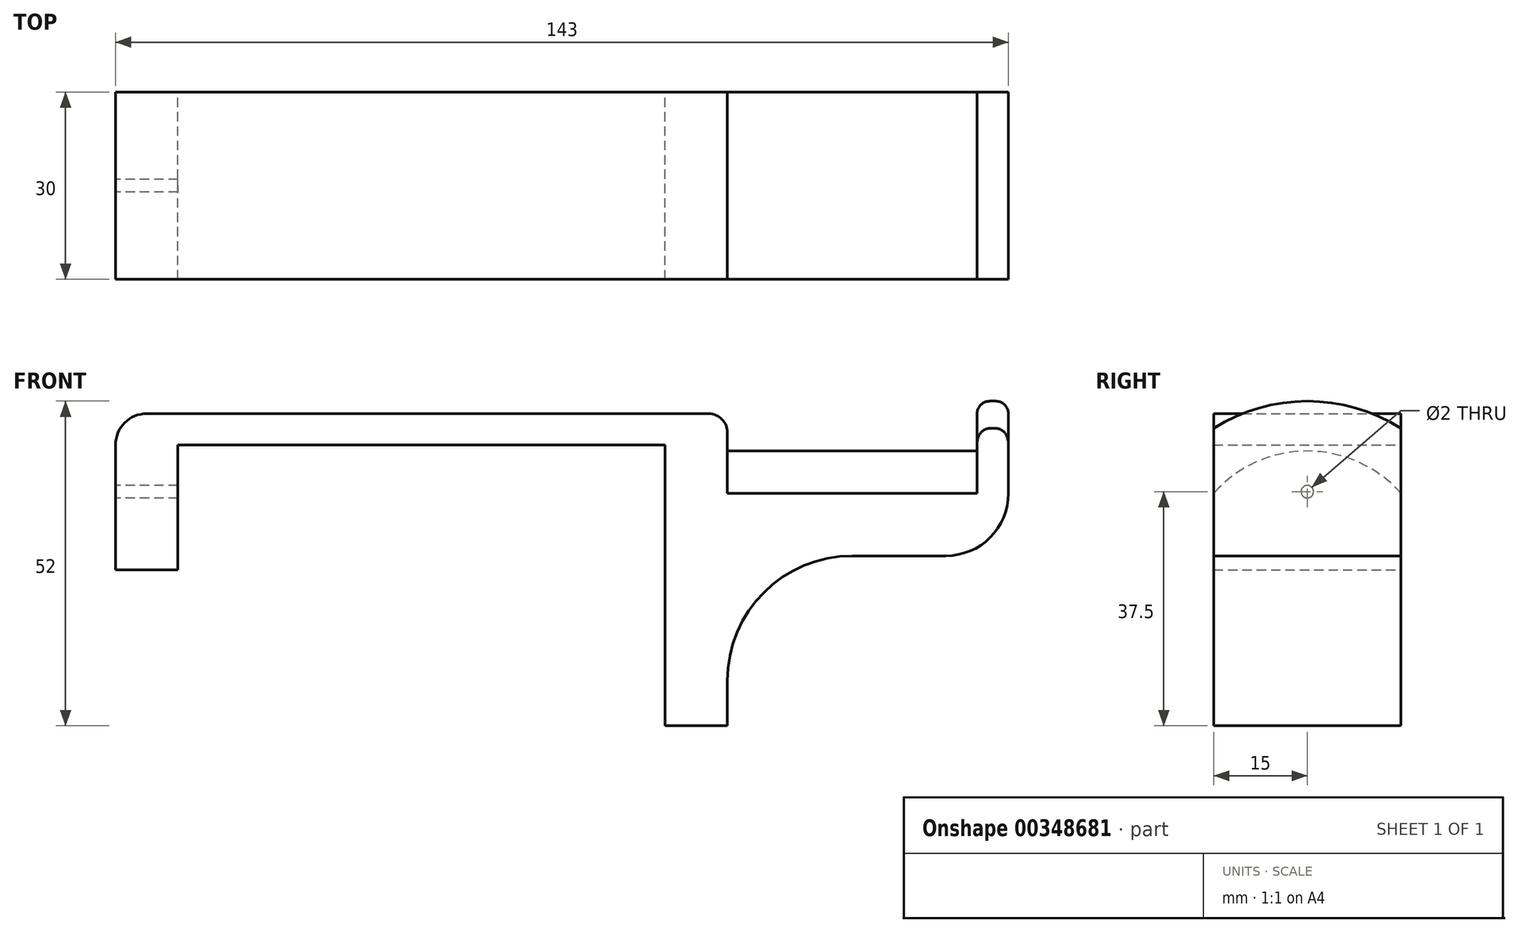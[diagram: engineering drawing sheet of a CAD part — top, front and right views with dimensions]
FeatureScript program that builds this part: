
annotation { "Feature Type Name" : "Feature", "Feature Type Description" : "" }
export const myFeature = defineFeature(function(context is Context, id is Id, definition is map)
    precondition{}
    {
        {
            var Q0;
            Q0=qCreatedBy(makeId("Front.planeOp"),FACE);
            var sketch = newSketch(context, id + "F0", { "sketchPlane" : qUnion([Q0])});
            skLineSegment(sketch, "E0", {"start": v(0, 0) * mm, "end": v(0, 45) * mm});
            skLineSegment(sketch, "E1", {"start": v(0, 45) * mm, "end": v(-78, 45) * mm});
            skLineSegment(sketch, "E2", {"start": v(-78, 45) * mm, "end": v(-78, 25) * mm});
            skLineSegment(sketch, "E3", {"start": v(-78, 25) * mm, "end": v(-88, 25) * mm});
            skLineSegment(sketch, "E4", {"start": v(-88, 25) * mm, "end": v(-88, 50) * mm});
            skLineSegment(sketch, "E5", {"start": v(-88, 50) * mm, "end": v(10, 50) * mm});
            skLineSegment(sketch, "E6", {"start": v(10, 50) * mm, "end": v(10, 0) * mm});
            skLineSegment(sketch, "E7", {"start": v(10, 0) * mm, "end": v(0, 0) * mm});
            skSolve(sketch);
        }
        {
            var Q0;
            Q0=makeQuery(id+"F0.imprint","IMPRINT",FACE,{"disambiguationData":[TD([[makeQuery(id+"F0.imprint","IMPRINT",EDGE,{"derivedFrom":sQuery(id+"F0.wireOp",EDGE,"E0")}),-1.0]])]});
            extrude(context, id + "F1", {"entities" : qUnion([Q0]), "depth" : 30 * mm});
        }
        {
            var Q0;
            Q0=makeQuery(id+"F1.opExtrude","SWEPT_FACE",FACE,{"disambiguationData":[OSD([sQuery(id+"F0.wireOp",EDGE,"E4")])]});
            var sketch = newSketch(context, id + "F2", { "sketchPlane" : qUnion([Q0])});
            skLineSegment(sketch, "E8", {"start": v(15, 50) * mm, "end": v(15, 25) * mm, "construction": true});
            skCircle(sketch, "E9", {"center": v(15, 37.5) * mm, "radius": 1 * mm});
            skSolve(sketch);
        }
        {
            var Q0;
            Q0=makeQuery(id+"F2.imprint","IMPRINT",FACE,{"disambiguationData":[TD([[makeQuery(id+"F2.imprint","IMPRINT",EDGE,{"derivedFrom":sQuery(id+"F2.wireOp",EDGE,"E9")}),1.0]])]});
            extrude(context, id + "F3", {"entities" : qUnion([Q0]), "operationType" : NewBodyOperationType.REMOVE, "endBound" : BoundingType.UP_TO_NEXT, "oppositeDirection" : true, "depth" : 25 * mm});
        }
        {
            var Q0;
            Q0=makeQuery(id+"F1.opExtrude","SWEPT_FACE",FACE,{"disambiguationData":[OSD([sQuery(id+"F0.wireOp",EDGE,"E6")])]});
            var sketch = newSketch(context, id + "F4", { "sketchPlane" : qUnion([Q0])});
            skArc(sketch, "E10", {"start": v(0, 37.23) * mm, "mid": v(-15, 44) * mm, "end": v(-30, 37.23) * mm});
            skLineSegment(sketch, "E11", {"start": v(-15, 24) * mm, "end": v(-15, 50) * mm, "construction": true});
            skLineSegment(sketch, "E12", {"start": v(-30, 37.23) * mm, "end": v(-30, 27.23) * mm});
            skLineSegment(sketch, "E13", {"start": v(-30, 27.23) * mm, "end": v(0, 27.23) * mm});
            skLineSegment(sketch, "E14", {"start": v(0, 27.23) * mm, "end": v(0, 37.23) * mm});
            skSolve(sketch);
        }
        {
            var Q0;
            Q0=makeQuery(id+"F4.imprint","IMPRINT",FACE,{"disambiguationData":[TD([[makeQuery(id+"F4.imprint","IMPRINT",EDGE,{"derivedFrom":sQuery(id+"F4.wireOp",EDGE,"E10")}),1.0]])]});
            extrude(context, id + "F5", {"entities" : qUnion([Q0]), "operationType" : NewBodyOperationType.ADD, "depth" : 40 * mm});
        }
        {
            var Q0;
            Q0=makeQuery(id+"F5.opExtrude","CAP_FACE",FACE,{"disambiguationData":[OSD([sQuery(id+"F4.wireOp",EDGE,"E10"),sQuery(id+"F4.wireOp",EDGE,"E12"),sQuery(id+"F4.wireOp",EDGE,"E13"),sQuery(id+"F4.wireOp",EDGE,"E14")])],"isStart":false});
            var sketch = newSketch(context, id + "F6", { "sketchPlane" : qUnion([Q0])});
            skArc(sketch, "E15.0", {"start": v(0, 47.64) * mm, "mid": v(-15, 52) * mm, "end": v(-30, 47.64) * mm});
            skLineSegment(sketch, "E16", {"start": v(-30, 27.23) * mm, "end": v(-30, 47.64) * mm});
            skLineSegment(sketch, "E17", {"start": v(0, 27.23) * mm, "end": v(0, 47.64) * mm});
            skLineSegment(sketch, "E18", {"start": v(0, 27.23) * mm, "end": v(-30, 27.23) * mm});
            skSolve(sketch);
        }
        {
            var Q0;
            {var subQ0=sQuery(id+"F6.wireOp",EDGE,"E15.0");Q0=makeQuery(id+"F6.imprint","IMPRINT",FACE,{"disambiguationData":[TD([[makeQuery(id+"F6.imprint","IMPRINT",EDGE,{"derivedFrom":subQ0}),1.0]])]});}
            var Q1;
            {var subQ2=sQuery(id+"F6.wireOp",EDGE,"E18");Q1=makeQuery(id+"F6.imprint","IMPRINT",FACE,{"disambiguationData":[TD([[makeQuery(id+"F6.imprint","IMPRINT",EDGE,{"derivedFrom":subQ2}),1.0]])]});}
            extrude(context, id + "F7", {"entities" : qUnion([Q0, Q1]), "operationType" : NewBodyOperationType.ADD, "depth" : 5 * mm});
        }
        {
            var Q0;
            Q0=makeQuery(id+"F5.opExtrude","CAP_EDGE",EDGE,{"disambiguationData":[OSD([sQuery(id+"F4.wireOp",EDGE,"E13")])],"isStart":true});
            fillet(context, id + "F8", {"entities" : qUnion([Q0]), "radius" : 20 * mm, "tangentPropagation" : true, "allowEdgeOverflow" : false});
        }
        {
            var Q0;
            Q0=makeQuery(id+"F5.opExtrude","CAP_EDGE",EDGE,{"disambiguationData":[OSD([sQuery(id+"F4.wireOp",EDGE,"E10")])],"isStart":true});
            var Q1;
            Q1=makeQuery(id+"F1.opExtrude","SWEPT_EDGE",EDGE,{"disambiguationData":[OSD([sQuery(id+"F0.wireOp",EDGE,"E5"),sQuery(id+"F0.wireOp",EDGE,"E6")])]});
            fillet(context, id + "F9", {"entities" : qUnion([Q0, Q1]), "radius" : 3 * mm, "tangentPropagation" : true, "allowEdgeOverflow" : false});
        }
        {
            var Q0;
            Q0=makeQuery(id+"F5.opExtrude","CAP_EDGE",EDGE,{"disambiguationData":[OSD([sQuery(id+"F4.wireOp",EDGE,"E10")])],"isStart":false});
            var Q1;
            Q1=makeQuery(id+"F7.opExtrude","CAP_EDGE",EDGE,{"disambiguationData":[OSD([sQuery(id+"F6.wireOp",EDGE,"E15.0")])],"isStart":true});
            var Q2;
            Q2=makeQuery(id+"F7.opExtrude","CAP_EDGE",EDGE,{"disambiguationData":[OSD([sQuery(id+"F6.wireOp",EDGE,"E15.0")])],"isStart":false});
            fillet(context, id + "F10", {"entities" : qUnion([Q0, Q1, Q2]), "radius" : 2 * mm, "tangentPropagation" : true, "allowEdgeOverflow" : false});
        }
        {
            var Q0;
            Q0=makeQuery(id+"F7.opExtrude","CAP_EDGE",EDGE,{"disambiguationData":[OSD([sQuery(id+"F6.wireOp",EDGE,"E18")])],"isStart":false});
            fillet(context, id + "F11", {"entities" : qUnion([Q0]), "radius" : 10 * mm, "tangentPropagation" : true, "allowEdgeOverflow" : false});
        }
        {
            var Q0;
            Q0=makeQuery(id+"F1.opExtrude","SWEPT_EDGE",EDGE,{"disambiguationData":[OSD([sQuery(id+"F0.wireOp",EDGE,"E4"),sQuery(id+"F0.wireOp",EDGE,"E5")])]});
            fillet(context, id + "F12", {"entities" : qUnion([Q0]), "radius" : 5 * mm, "tangentPropagation" : true, "allowEdgeOverflow" : false});
        }
    });
